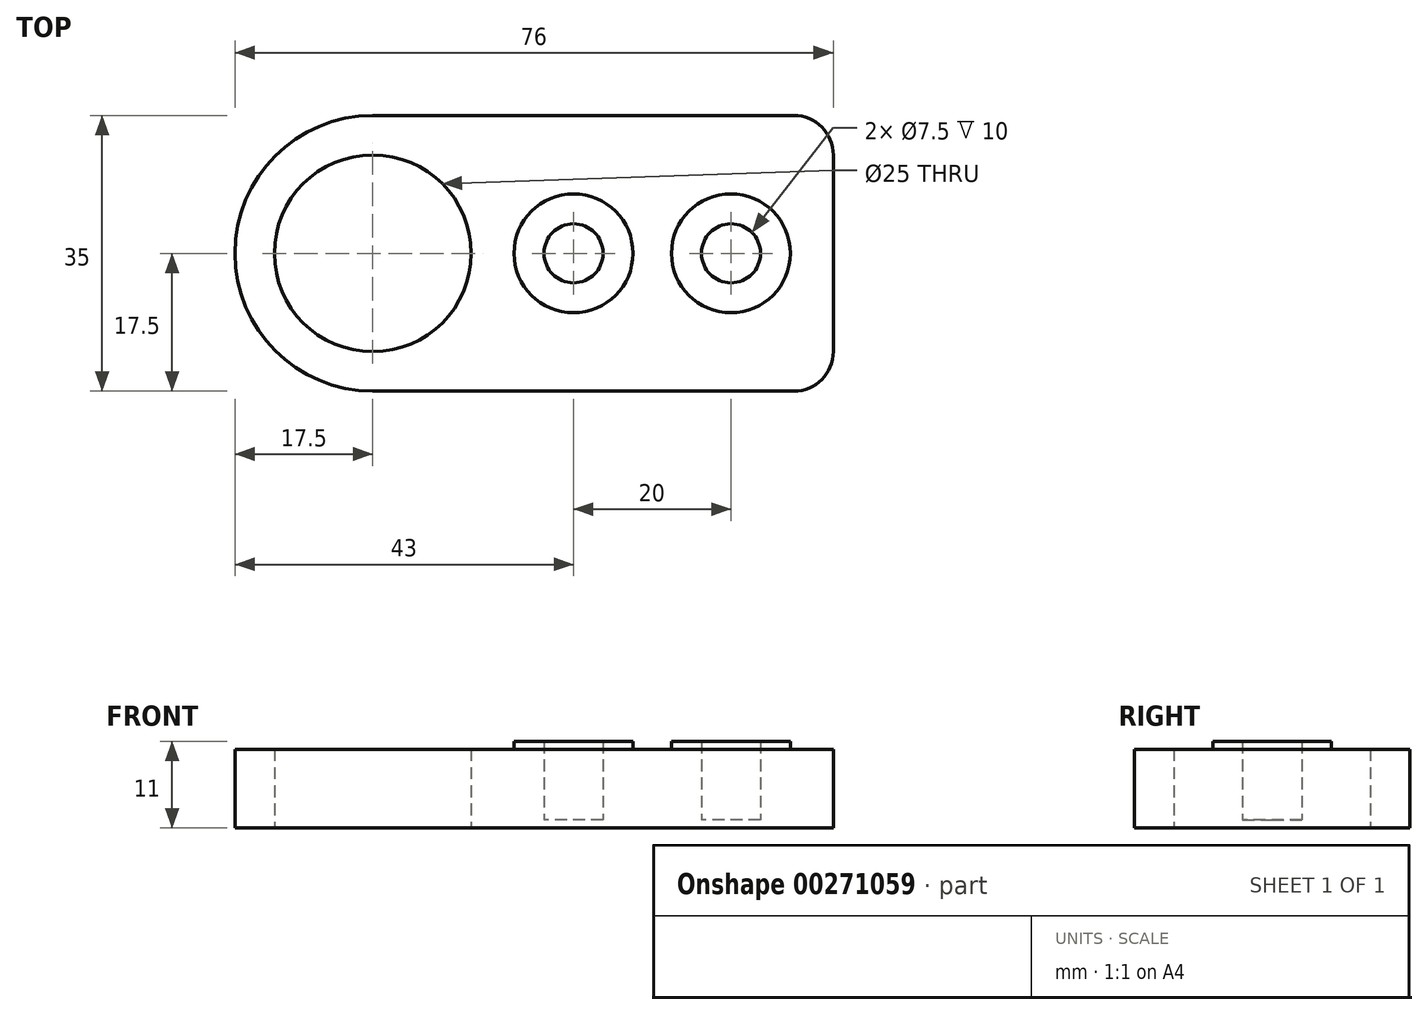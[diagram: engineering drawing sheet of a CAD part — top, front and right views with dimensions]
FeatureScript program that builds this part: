
annotation { "Feature Type Name" : "Feature", "Feature Type Description" : "" }
export const myFeature = defineFeature(function(context is Context, id is Id, definition is map)
    precondition{}
    {
        {
            var Q0;
            Q0=qCreatedBy(makeId("Top.planeOp"),FACE);
            var sketch = newSketch(context, id + "F0", { "sketchPlane" : qUnion([Q0])});
            skLineSegment(sketch, "E0.bottom", {"start": v(17.5, 0) * mm, "end": v(71, 0) * mm});
            skLineSegment(sketch, "E0.top", {"start": v(17.5, 35) * mm, "end": v(71, 35) * mm});
            skLineSegment(sketch, "E0.left", {"start": v(0, 17.5) * mm, "end": v(0, 17.5) * mm});
            skLineSegment(sketch, "E0.right", {"start": v(76, 5) * mm, "end": v(76, 30) * mm});
            skLineSegment(sketch, "E1.bottom", {"start": v(0, 0) * mm, "end": v(17.5, 0) * mm, "construction": true});
            skLineSegment(sketch, "E1.top", {"start": v(0, 17.5) * mm, "end": v(17.5, 17.5) * mm, "construction": true});
            skLineSegment(sketch, "E1.left", {"start": v(0, 0) * mm, "end": v(0, 17.5) * mm, "construction": true});
            skLineSegment(sketch, "E1.right", {"start": v(17.5, 0) * mm, "end": v(17.5, 17.5) * mm, "construction": true});
            skCircle(sketch, "E2", {"center": v(17.5, 17.5) * mm, "radius": 12.5 * mm});
            skPoint(sketch, "E3.visualSharp", {"position": v(0, 0) * mm});
            skArc(sketch, "E3.filletArc", {"start": v(0, 17.5) * mm, "mid": v(5.13, 5.13) * mm, "end": v(17.5, 0) * mm});
            skPoint(sketch, "E4.visualSharp", {"position": v(0, 35) * mm});
            skArc(sketch, "E4.filletArc", {"start": v(17.5, 35) * mm, "mid": v(5.13, 29.87) * mm, "end": v(0, 17.5) * mm});
            skPoint(sketch, "E5.visualSharp", {"position": v(76, 35) * mm});
            skArc(sketch, "E5.filletArc", {"start": v(76, 30) * mm, "mid": v(74.54, 33.54) * mm, "end": v(71, 35) * mm});
            skPoint(sketch, "E6.visualSharp", {"position": v(76, 0) * mm});
            skArc(sketch, "E6.filletArc", {"start": v(71, 0) * mm, "mid": v(74.54, 1.46) * mm, "end": v(76, 5) * mm});
            skSolve(sketch);
        }
        {
            var Q0;
            Q0=makeQuery(id+"F0.imprint","IMPRINT",FACE,{"disambiguationData":[TD([[makeQuery(id+"F0.imprint","IMPRINT",EDGE,{"derivedFrom":sQuery(id+"F0.wireOp",EDGE,"E0.bottom")}),1.0]])]});
            extrude(context, id + "F1", {"entities" : qUnion([Q0]), "depth" : 10 * mm});
        }
        {
            var Q0;
            Q0=makeQuery(id+"F1.opExtrude","CAP_FACE",FACE,{"disambiguationData":[OSD([sQuery(id+"F0.wireOp",EDGE,"E0.bottom"),sQuery(id+"F0.wireOp",EDGE,"E0.top"),sQuery(id+"F0.wireOp",EDGE,"E0.right"),sQuery(id+"F0.wireOp",EDGE,"E2"),sQuery(id+"F0.wireOp",EDGE,"E3.filletArc"),sQuery(id+"F0.wireOp",EDGE,"E4.filletArc"),sQuery(id+"F0.wireOp",EDGE,"E5.filletArc"),sQuery(id+"F0.wireOp",EDGE,"E6.filletArc")])],"isStart":false});
            var sketch = newSketch(context, id + "F2", { "sketchPlane" : qUnion([Q0])});
            skLineSegment(sketch, "E7.bottom", {"start": v(0, 0) * mm, "end": v(43, 0) * mm, "construction": true});
            skLineSegment(sketch, "E7.top", {"start": v(0, 17.5) * mm, "end": v(43, 17.5) * mm, "construction": true});
            skLineSegment(sketch, "E7.left", {"start": v(0, 0) * mm, "end": v(0, 17.5) * mm, "construction": true});
            skLineSegment(sketch, "E7.right", {"start": v(43, 0) * mm, "end": v(43, 17.5) * mm, "construction": true});
            skCircle(sketch, "E8", {"center": v(43, 17.5) * mm, "radius": 7.55 * mm});
            skCircle(sketch, "E9", {"center": v(43, 17.5) * mm, "radius": 3.75 * mm});
            skLineSegment(sketch, "E10", {"start": v(43, 17.5) * mm, "end": v(63, 17.5) * mm, "construction": true});
            skCircle(sketch, "E11", {"center": v(63, 17.5) * mm, "radius": 3.75 * mm});
            skCircle(sketch, "E12", {"center": v(63, 17.5) * mm, "radius": 7.55 * mm});
            skSolve(sketch);
        }
        {
            var Q0;
            Q0=makeQuery(id+"F2.imprint","IMPRINT",FACE,{"disambiguationData":[TD([[makeQuery(id+"F2.imprint","IMPRINT",EDGE,{"derivedFrom":sQuery(id+"F2.wireOp",EDGE,"E8")}),1.0]])]});
            var Q1;
            Q1=makeQuery(id+"F2.imprint","IMPRINT",FACE,{"disambiguationData":[TD([[makeQuery(id+"F2.imprint","IMPRINT",EDGE,{"derivedFrom":sQuery(id+"F2.wireOp",EDGE,"E11")}),-1.0]])]});
            extrude(context, id + "F3", {"entities" : qUnion([Q0, Q1]), "operationType" : NewBodyOperationType.ADD, "depth" : 1 * mm});
        }
        {
            var Q0;
            Q0=makeQuery(id+"F3.boolean.opBoolean","SPLIT",FACE,{"disambiguationData":[TD([makeQuery(id+"F3.opExtrude","SWEPT_FACE",FACE,{"disambiguationData":[OSD([sQuery(id+"F2.wireOp",EDGE,"E9")])]})])],"derivedFrom":makeQuery(id+"F1.opExtrude","CAP_FACE",FACE,{"disambiguationData":[OSD([sQuery(id+"F0.wireOp",EDGE,"E0.bottom"),sQuery(id+"F0.wireOp",EDGE,"E0.top"),sQuery(id+"F0.wireOp",EDGE,"E0.right"),sQuery(id+"F0.wireOp",EDGE,"E2"),sQuery(id+"F0.wireOp",EDGE,"E3.filletArc"),sQuery(id+"F0.wireOp",EDGE,"E4.filletArc"),sQuery(id+"F0.wireOp",EDGE,"E5.filletArc"),sQuery(id+"F0.wireOp",EDGE,"E6.filletArc")])],"isStart":false})});
            var Q1;
            Q1=makeQuery(id+"F3.boolean.opBoolean","SPLIT",FACE,{"disambiguationData":[TD([makeQuery(id+"F3.opExtrude","SWEPT_FACE",FACE,{"disambiguationData":[OSD([sQuery(id+"F2.wireOp",EDGE,"E11")])]})])],"derivedFrom":makeQuery(id+"F1.opExtrude","CAP_FACE",FACE,{"disambiguationData":[OSD([sQuery(id+"F0.wireOp",EDGE,"E0.bottom"),sQuery(id+"F0.wireOp",EDGE,"E0.top"),sQuery(id+"F0.wireOp",EDGE,"E0.right"),sQuery(id+"F0.wireOp",EDGE,"E2"),sQuery(id+"F0.wireOp",EDGE,"E3.filletArc"),sQuery(id+"F0.wireOp",EDGE,"E4.filletArc"),sQuery(id+"F0.wireOp",EDGE,"E5.filletArc"),sQuery(id+"F0.wireOp",EDGE,"E6.filletArc")])],"isStart":false})});
            extrude(context, id + "F4", {"entities" : qUnion([Q0, Q1]), "operationType" : NewBodyOperationType.REMOVE, "oppositeDirection" : true, "depth" : 9 * mm});
        }
    });
